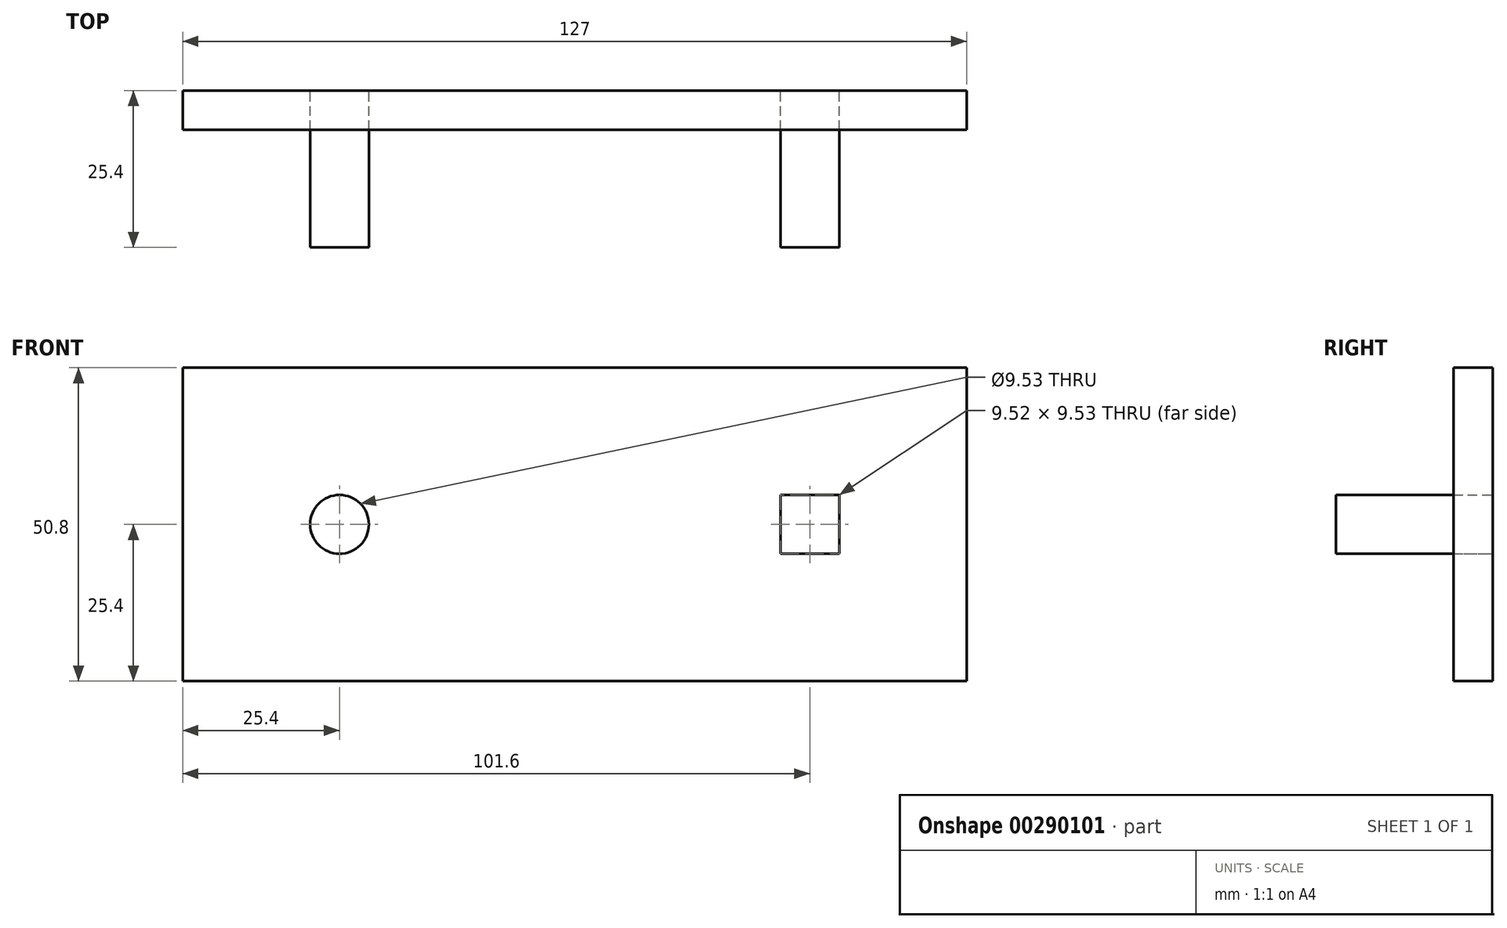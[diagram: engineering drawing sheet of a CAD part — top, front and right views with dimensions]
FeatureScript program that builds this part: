
annotation { "Feature Type Name" : "Feature", "Feature Type Description" : "" }
export const myFeature = defineFeature(function(context is Context, id is Id, definition is map)
    precondition{}
    {
        {
            var Q0;
            Q0=qCreatedBy(makeId("Front.planeOp"),FACE);
            var sketch = newSketch(context, id + "F0", { "sketchPlane" : qUnion([Q0])});
            skLineSegment(sketch, "E0.bottom", {"start": v(0, 0) * mm, "end": v(127, 0) * mm});
            skLineSegment(sketch, "E0.top", {"start": v(0, 50.8) * mm, "end": v(127, 50.8) * mm});
            skLineSegment(sketch, "E0.left", {"start": v(0, 0) * mm, "end": v(0, 50.8) * mm});
            skLineSegment(sketch, "E0.right", {"start": v(127, 0) * mm, "end": v(127, 50.8) * mm});
            skCircle(sketch, "E1", {"center": v(25.4, 25.4) * mm, "radius": 4.76 * mm});
            skLineSegment(sketch, "E2.bottom", {"start": v(96.84, 20.64) * mm, "end": v(106.36, 20.64) * mm});
            skLineSegment(sketch, "E2.top", {"start": v(96.84, 30.16) * mm, "end": v(106.36, 30.16) * mm});
            skLineSegment(sketch, "E2.left", {"start": v(96.84, 20.64) * mm, "end": v(96.84, 30.16) * mm});
            skLineSegment(sketch, "E2.right", {"start": v(106.36, 20.64) * mm, "end": v(106.36, 30.16) * mm});
            skPoint(sketch, "E2.middle", {"position": v(101.6, 25.4) * mm});
            skSolve(sketch);
        }
        {
            var Q0;
            Q0=makeQuery(id+"F0.imprint","IMPRINT",FACE,{"disambiguationData":[TD([[makeQuery(id+"F0.imprint","IMPRINT",EDGE,{"derivedFrom":sQuery(id+"F0.wireOp",EDGE,"E2.bottom")}),1.0]])]});
            var Q1;
            Q1=makeQuery(id+"F0.imprint","IMPRINT",FACE,{"disambiguationData":[TD([[makeQuery(id+"F0.imprint","IMPRINT",EDGE,{"derivedFrom":sQuery(id+"F0.wireOp",EDGE,"E1")}),1.0]])]});
            extrude(context, id + "F1", {"entities" : qUnion([Q0, Q1]), "depth" : 25.4 * mm});
        }
        {
            var Q0;
            Q0=makeQuery(id+"F0.imprint","IMPRINT",FACE,{"disambiguationData":[TD([[makeQuery(id+"F0.imprint","IMPRINT",EDGE,{"derivedFrom":sQuery(id+"F0.wireOp",EDGE,"E0.bottom")}),1.0]])]});
            extrude(context, id + "F2", {"entities" : qUnion([Q0]), "depth" : 6.35 * mm});
        }
    });
